# Revit family: BFX-DIR-DSD-ME-Ceiling
name_source: partatom
category: Lighting Fixtures
revit_build: Autodesk Revit 2018 (Build: 20180423_1000(x64)
units: mm (PartAtom-declared; Revit-internal decimal feet)

## family parameters
Cut with Voids When Loaded = No
Host = Face
Light Source = No
OmniClass Number = 23.35.47.15
OmniClass Title = Exit Illuminated Signs
Part Type = Normal
Room Calculation Point = No
Round Connector Dimension = Use Diameter
Shared = No

## types (8) — shared parameters
Apparent Load = 3.0 W
Depth = 60 mm  [stored 0.19685 ft]
Height = 125 mm
Indication lamp = PL_Red_255-000-000
Top Material = PL_White_255-255-255
zero-valued in all types: DSD.BFX.Height, DSD.BFX.Length, DSD.BFX.Width

## per-type parameters (varying)
| type | 294 EXIT SIGN DIRECTION_2 | Default Elevation | Down | Left | Length | Load Classification | Right | Up |
| 650Lx125Wx60H (Up) | 294 EXIT SIGN DIRECTION_2 : 560x180x12mm | 1219 mm | No | No | 650 mm | Other | No | Yes |
| 540Lx125Wx60H (Up) | 294 EXIT SIGN DIRECTION_2 : 460x175x12mm | 1219 mm | No | No | 540 mm  [stored 1.77165 ft] | Lighting | No | Yes |
| 540Lx125Wx60H (Down) | 294 EXIT SIGN DIRECTION_2 : 460x175x12mm | 0 mm  [stored 0 ft] | Yes | No | 540 mm  [stored 1.77165 ft] | Lighting | No | No |
| 540Lx125Wx60H (Right) | 294 EXIT SIGN DIRECTION_2 : 460x175x12mm | 1219 mm | No | No | 540 mm  [stored 1.77165 ft] | Lighting | Yes | No |
| 540Lx125Wx60H (Left) | 294 EXIT SIGN DIRECTION_2 : 460x175x12mm | 1219 mm | No | Yes | 540 mm  [stored 1.77165 ft] | Lighting | No | No |
| 650Lx125Wx60H (Down) | 294 EXIT SIGN DIRECTION_2 : 560x180x12mm | 1219 mm | Yes | No | 650 mm | Other | No | No |
| 650Lx125Wx60H (Right) | 294 EXIT SIGN DIRECTION_2 : 560x180x12mm | 1219 mm | No | No | 650 mm | Other | Yes | No |
| 650Lx125Wx60H (Left) | 294 EXIT SIGN DIRECTION_2 : 560x180x12mm | 1219 mm | No | Yes | 650 mm | Other | No | No |

note: [stored X ft] marks values corroborated as IEEE doubles in the binary element streams (Revit-internal decimal feet)

## geometry (parser evidence)
native form markers: Sweep x13
no freeform markers — native parametric forms only
